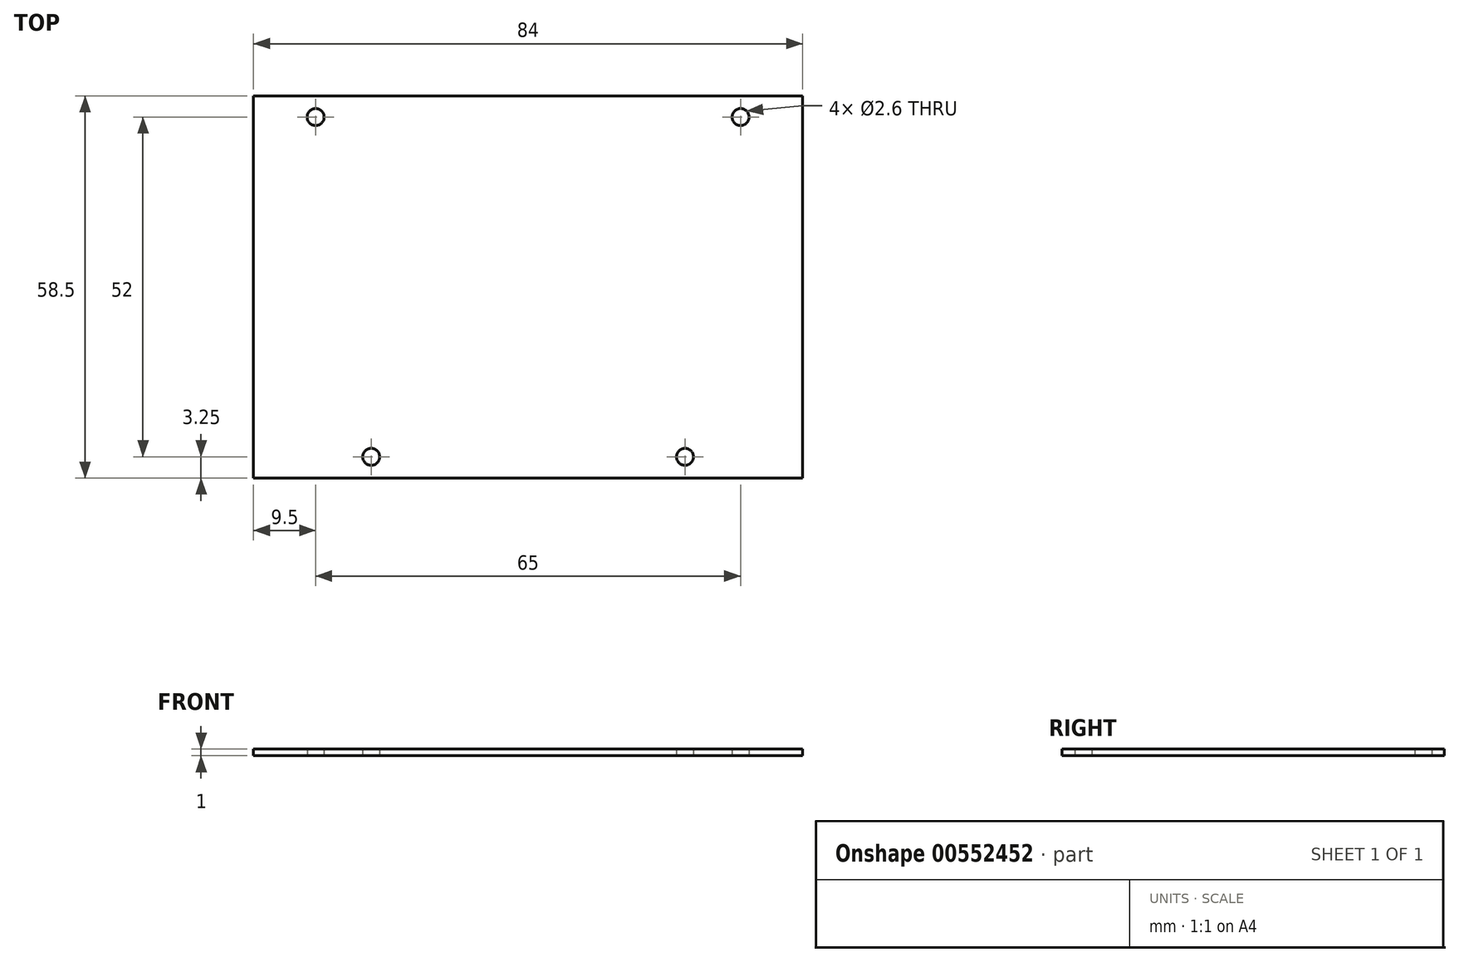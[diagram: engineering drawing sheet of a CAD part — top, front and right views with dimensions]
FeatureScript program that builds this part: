
annotation { "Feature Type Name" : "Feature", "Feature Type Description" : "" }
export const myFeature = defineFeature(function(context is Context, id is Id, definition is map)
    precondition{}
    {
        {
            var Q0;
            Q0=qCreatedBy(makeId("Top.planeOp"),FACE);
            var sketch = newSketch(context, id + "F0", { "sketchPlane" : qUnion([Q0])});
            skLineSegment(sketch, "E0.bottom", {"start": v(-42, 29.25) * mm, "end": v(42, 29.25) * mm});
            skLineSegment(sketch, "E0.top", {"start": v(-42, -29.25) * mm, "end": v(42, -29.25) * mm});
            skLineSegment(sketch, "E0.left", {"start": v(-42, 29.25) * mm, "end": v(-42, -29.25) * mm});
            skLineSegment(sketch, "E0.right", {"start": v(42, 29.25) * mm, "end": v(42, -29.25) * mm});
            skCircle(sketch, "E1", {"center": v(-32.5, 26) * mm, "radius": 1.3 * mm});
            skCircle(sketch, "E2", {"center": v(32.5, 26) * mm, "radius": 1.3 * mm});
            skCircle(sketch, "E3", {"center": v(-24, -26) * mm, "radius": 1.3 * mm});
            skCircle(sketch, "E4", {"center": v(24, -26) * mm, "radius": 1.3 * mm});
            skSolve(sketch);
        }
        {
            var Q0;
            Q0 = qSketchRegion(id + "F0", true);
            extrude(context, id + "F1", {"entities" : qUnion([Q0]), "depth" : 1 * mm, "offsetDistance" : 25 * mm});
        }
    });
